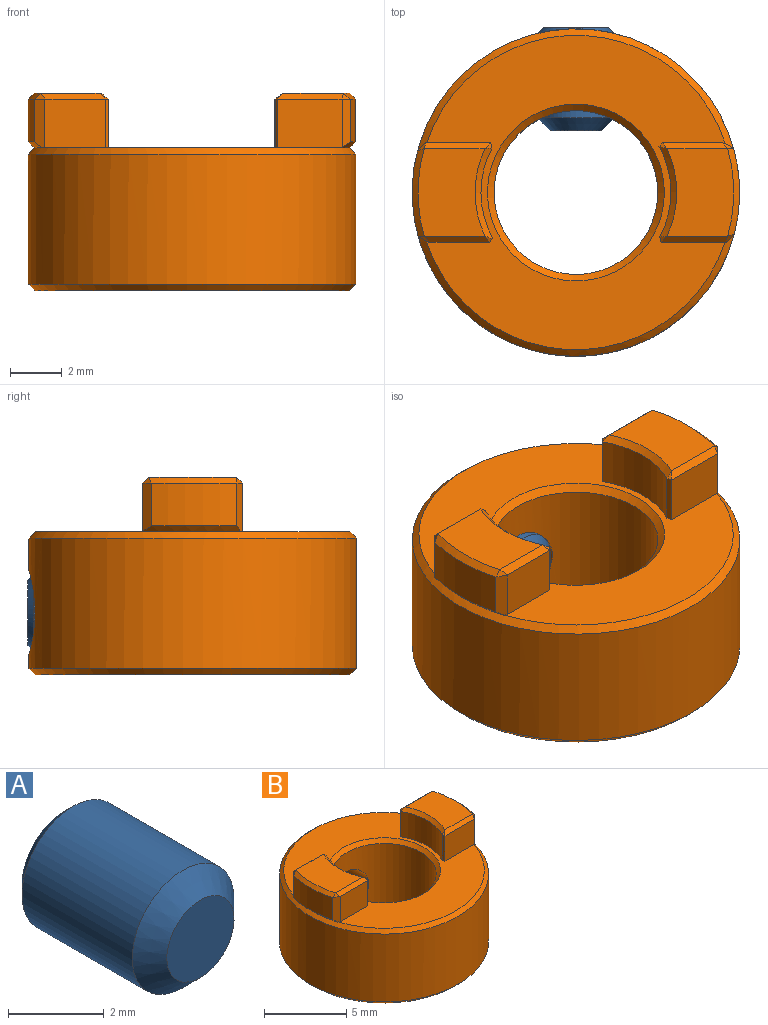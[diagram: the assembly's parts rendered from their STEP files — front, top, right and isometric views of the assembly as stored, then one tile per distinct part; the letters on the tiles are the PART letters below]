
ASSEMBLY  parts=2 mates=1
PART A: 18 faces, bbox 3x4x3 mm
  f0: cylinder r=1.5mm len=3.25mm, axis (0,1,0), area 30.6mm2, adj f16,f17
  f1: plane 1.98x1.98mm, normal (0,-1,0), area 3.1mm2, adj f17
  f2: plane 2.52x2.52mm, normal (0,1,0), area 2.6mm2, adj f3,f4,f5,f6,f7,f8,f16
  f3: cone r=0.87mm half-angle=45deg, axis (0,1,0), area 0.1mm2, adj f2,f10
  f4: cone r=0.87mm half-angle=45deg, axis (0,1,0), area 0.1mm2, adj f2,f11
  f5: cone r=0.87mm half-angle=45deg, axis (0,1,0), area 0.1mm2, adj f2,f12
  f6: cone r=0.87mm half-angle=45deg, axis (0,1,0), area 0.1mm2, adj f2,f13
  f7: cone r=0.87mm half-angle=45deg, axis (0,1,0), area 0.1mm2, adj f2,f14
  f8: cone r=0.87mm half-angle=45deg, axis (0,1,0), area 0.1mm2, adj f2,f15
  f9: plane 1.73x1.5mm, normal (0,1,0), area 1.9mm2, adj f10,f11,f12,f13,f14,f15
  f10: plane 0.9x0.75mm, normal (-0.87,0,-0.5), area 0.7mm2, adj f3,f9,f11,f15
  f11: plane 0.9x0.75mm, normal (-0.87,0,0.5), area 0.7mm2, adj f4,f9,f10,f12
  f12: plane 0.9x0.87mm, normal (0,0,1), area 0.7mm2, adj f5,f9,f11,f13
  f13: plane 0.9x0.75mm, normal (0.87,0,0.5), area 0.7mm2, adj f6,f9,f12,f14
  f14: plane 0.9x0.75mm, normal (0.87,0,-0.5), area 0.7mm2, adj f7,f9,f13,f15
  f15: plane 0.9x0.87mm, normal (0,0,-1), area 0.7mm2, adj f8,f9,f10,f14
  f16: cone r=1.26mm half-angle=45deg, axis (0,-1,0), area 2.9mm2, adj f0,f2
  f17: cone r=1.5mm half-angle=45deg, axis (0,1,0), area 5.6mm2, adj f0,f1
PART B: 48 faces, bbox 12.7x12.7x7.7 mm
  f0: cylinder r=6.35mm len=12.7mm, axis (0,0,1), area 192.5mm2, adj f4,f5,f45
  f1: cylinder r=3.17mm len=6.35mm, axis (0,0,1), area 93.4mm2, adj f44,f46,f47
  f2: plane 12.19x11.6mm, normal (0,0,1), area 60.7mm2, adj f4,f7,f8,f10,f14,f18,f21,f25
  f3: plane 12.19x12.19mm, normal (0,0,-1), area 79.8mm2, adj f5,f46
  f4: cone r=6.1mm half-angle=45deg, axis (0,0,-1), area 14mm2, adj f0,f2,f6,f27
  f5: cone r=6.35mm half-angle=45deg, axis (0,0,1), area 14mm2, adj f0,f3
  f6: plane 3.81x0.34mm, normal (0,0,-1), area 0.1mm2, adj f4,f8,f15,f18
  f7: cylinder r=3.68mm len=3.51mm, axis (0,0,-1), area 6.9mm2, adj f2,f14,f20,f21
  f8: plane 2.52x1.88mm, normal (0,-1,0), area 4.7mm2, adj f2,f6,f12,f13,f14,f15
  f9: cylinder r=6.35mm len=3.32mm, axis (0,0,-1), area 5.6mm2, adj f12,f15,f18,f19
  f10: plane 2.33x1.88mm, normal (0,1,0), area 4.4mm2, adj f2,f18,f21,f24
  f11: plane 3.4x2.6mm, normal (0,0,1), area 7.7mm2, adj f13,f19,f20,f24
  f12: plane 1.88x0.33mm, normal (0.71,-0.71,0), area 0.8mm2, adj f8,f9,f15,f16
  f13: plane 2.58x0.23mm, normal (0,-0.71,0.71), area 0.8mm2, adj f8,f11,f16,f17
  f14: plane 1.88x0.21mm, normal (-0.97,-0.23,0), area 0.4mm2, adj f2,f7,f8,f17
  f15: cone r=6.35mm half-angle=45deg, axis (0,0,1), area 1.2mm2, adj f6,f8,f9,f12,f18
  f16: plane 0.33x0.33mm, normal (0.63,-0.63,0.46), area 0.1mm2, adj f12,f13,f19
  f17: plane 0.27x0.23mm, normal (-0.63,-0.15,0.76), area 0mm2, adj f13,f14,f20
  f18: plane 1.88x0.42mm, normal (0.46,0.89,0), area 0.8mm2, adj f2,f6,f9,f10,f15,f22
  f19: cone r=6.12mm half-angle=45deg, axis (0,0,-1), area 1.1mm2, adj f9,f11,f16,f22
  f20: cone r=3.91mm half-angle=45deg, axis (0,0,1), area 1.2mm2, adj f7,f11,f17,f23
  f21: plane 1.88x0.14mm, normal (-0.71,0.71,0), area 0.4mm2, adj f2,f7,f10,f23
  f22: plane 0.42x0.23mm, normal (0.41,0.79,0.46), area 0.1mm2, adj f18,f19,f24
  f23: plane 0.31x0.23mm, normal (-0.45,0.45,0.77), area 0mm2, adj f20,f21,f24
  f24: plane 2.52x0.23mm, normal (0,0.71,0.71), area 0.8mm2, adj f10,f11,f22,f23
  f25: cylinder r=3.68mm len=3.51mm, axis (0,0,-1), area 6.9mm2, adj f2,f38,f40,f41
  f26: plane 2.33x1.88mm, normal (0,-1,0), area 4.4mm2, adj f2,f34,f41,f43
  f27: plane 3.81x0.34mm, normal (0,0,-1), area 0.1mm2, adj f4,f28,f33,f34
  f28: plane 2.52x1.88mm, normal (0,1,0), area 4.7mm2, adj f2,f27,f32,f33,f37,f38
  f29: cylinder r=6.35mm len=3.32mm, axis (0,0,-1), area 5.6mm2, adj f32,f33,f34,f36
  f30: plane 3.4x2.6mm, normal (0,0,1), area 7.7mm2, adj f36,f37,f40,f43
  f31: plane 0.33x0.33mm, normal (-0.63,0.63,0.46), area 0.1mm2, adj f32,f36,f37
  f32: plane 1.88x0.33mm, normal (-0.71,0.71,0), area 0.8mm2, adj f28,f29,f31,f33
  f33: cone r=6.35mm half-angle=45deg, axis (0,0,1), area 1.2mm2, adj f27,f28,f29,f32,f34
  f34: plane 1.88x0.42mm, normal (-0.46,-0.89,0), area 0.8mm2, adj f2,f26,f27,f29,f33,f35
  f35: plane 0.42x0.23mm, normal (-0.41,-0.79,0.46), area 0.1mm2, adj f34,f36,f43
  f36: cone r=6.12mm half-angle=45deg, axis (0,0,-1), area 1.1mm2, adj f29,f30,f31,f35
  f37: plane 2.58x0.23mm, normal (0,0.71,0.71), area 0.8mm2, adj f28,f30,f31,f39
  f38: plane 1.88x0.21mm, normal (0.97,0.23,0), area 0.4mm2, adj f2,f25,f28,f39
  f39: plane 0.27x0.23mm, normal (0.63,0.15,0.76), area 0mm2, adj f37,f38,f40
  f40: cone r=3.91mm half-angle=45deg, axis (0,0,1), area 1.2mm2, adj f25,f30,f39,f42
  f41: plane 1.88x0.14mm, normal (0.71,-0.71,0), area 0.4mm2, adj f2,f25,f26,f42
  f42: plane 0.31x0.23mm, normal (0.45,-0.45,0.77), area 0mm2, adj f40,f41,f43
  f43: plane 2.52x0.23mm, normal (0,-0.71,0.71), area 0.8mm2, adj f26,f30,f35,f42
  f44: cylinder r=1.5mm len=3mm, axis (0,-1,0), area 28mm2, adj f1,f45
  f45: bspline ~3.4x3.29mm, area 2.7mm2, adj f0,f44
  f46: cone r=3.43mm half-angle=45deg, axis (0,0,-1), area 7.5mm2, adj f1,f3
  f47: cone r=3.17mm half-angle=45deg, axis (0,0,1), area 7.5mm2, adj f1,f2
PLACE A t=(-2.19,-2.92,1.54)mm
PLACE B t=(-2.19,-2.97,1.54)mm
MATE fastened A.f0 <-> B.f44  axis (0,1,0) through (-2.19,3.19,-3.98)mm
